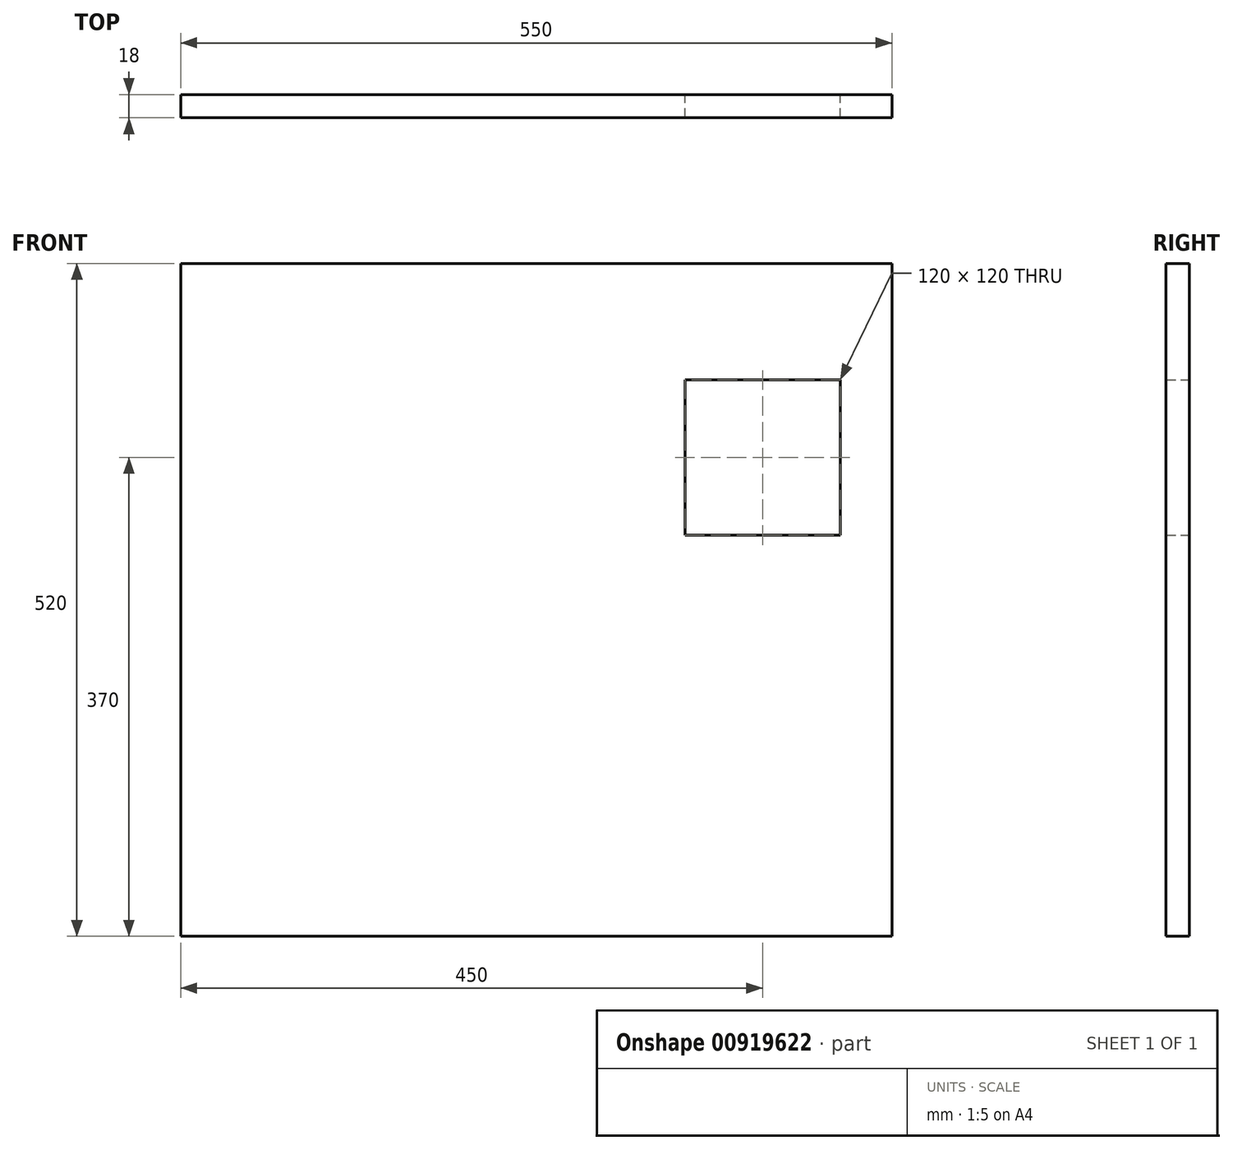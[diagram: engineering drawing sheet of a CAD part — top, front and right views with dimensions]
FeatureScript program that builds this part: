
annotation { "Feature Type Name" : "Feature", "Feature Type Description" : "" }
export const myFeature = defineFeature(function(context is Context, id is Id, definition is map)
    precondition{}
    {
        {
            var Q0;
            Q0=qCreatedBy(makeId("Front.planeOp"),FACE);
            var sketch = newSketch(context, id + "F0", { "sketchPlane" : qUnion([Q0])});
            skLineSegment(sketch, "E0.rect.bottom", {"start": v(275, -260) * mm, "end": v(-275, -260) * mm});
            skLineSegment(sketch, "E0.rect.top", {"start": v(275, 260) * mm, "end": v(-275, 260) * mm});
            skLineSegment(sketch, "E0.rect.left", {"start": v(275, -260) * mm, "end": v(275, 260) * mm});
            skLineSegment(sketch, "E0.rect.right", {"start": v(-275, -260) * mm, "end": v(-275, 260) * mm});
            skPoint(sketch, "E0.rect.middle", {"position": v(0, 0) * mm});
            skLineSegment(sketch, "E1", {"start": v(-275, -210) * mm, "end": v(275, -210) * mm});
            skLineSegment(sketch, "E2", {"start": v(-275, 210) * mm, "end": v(275, 210) * mm});
            skLineSegment(sketch, "E3.bottom", {"start": v(115, 170) * mm, "end": v(235, 170) * mm});
            skLineSegment(sketch, "E3.top", {"start": v(115, 50) * mm, "end": v(235, 50) * mm});
            skLineSegment(sketch, "E3.left", {"start": v(115, 170) * mm, "end": v(115, 50) * mm});
            skLineSegment(sketch, "E3.right", {"start": v(235, 170) * mm, "end": v(235, 50) * mm});
            skSolve(sketch);
        }
        {
            var Q0;
            Q0=qSketchRegion(id+"F0",true);
            extrude(context, id + "F1", {"entities" : qUnion([Q0]), "depth" : 18 * mm});
        }
    });
